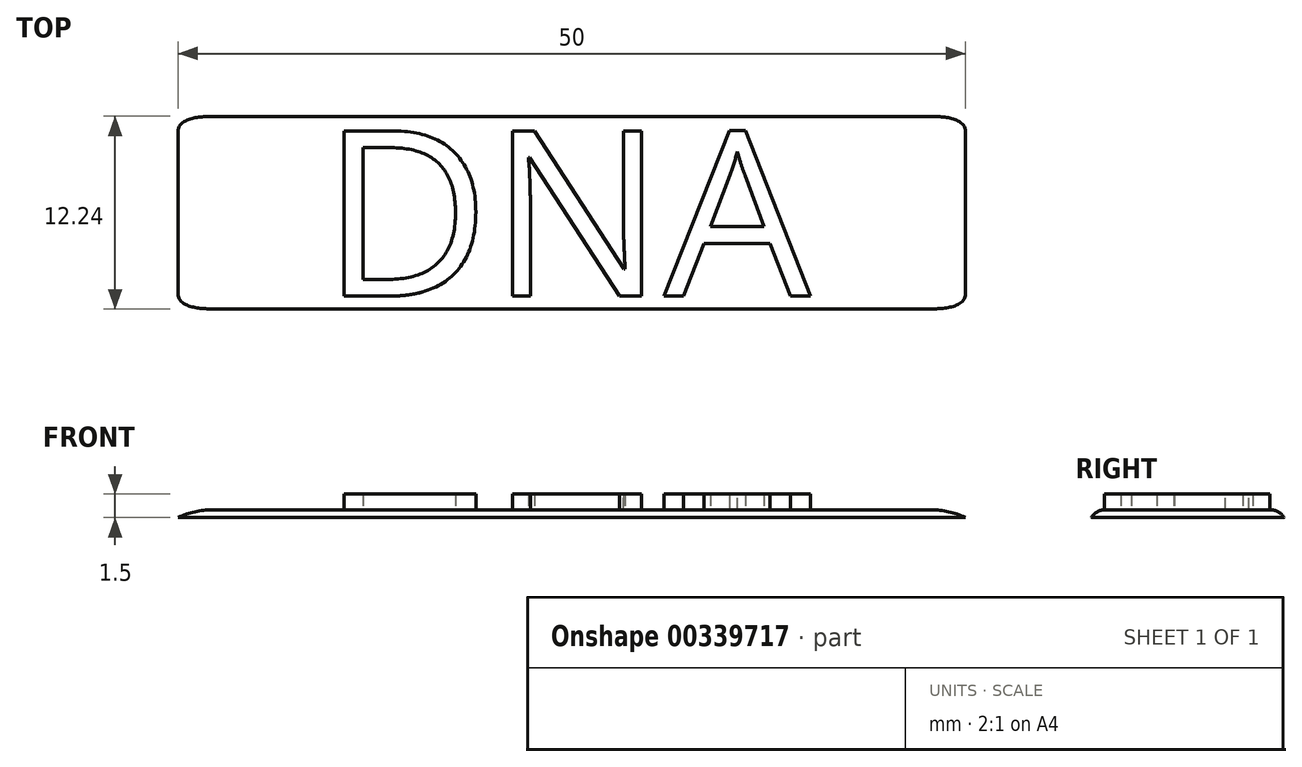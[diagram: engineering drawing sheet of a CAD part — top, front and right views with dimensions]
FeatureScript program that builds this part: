
annotation { "Feature Type Name" : "Feature", "Feature Type Description" : "" }
export const myFeature = defineFeature(function(context is Context, id is Id, definition is map)
    precondition{}
    {
        {
            var Q0;
            Q0=qCreatedBy(makeId("Top.planeOp"),FACE);
            var sketch = newSketch(context, id + "F0", { "sketchPlane" : qUnion([Q0])});
            skLineSegment(sketch, "E0.bottom", {"start": v(25, 6.25) * mm, "end": v(-25, 6.25) * mm});
            skLineSegment(sketch, "E0.top", {"start": v(25, -6.25) * mm, "end": v(-25, -6.25) * mm});
            skLineSegment(sketch, "E0.left", {"start": v(25, 6.25) * mm, "end": v(25, -6.25) * mm});
            skLineSegment(sketch, "E0.right", {"start": v(-25, 6.25) * mm, "end": v(-25, -6.25) * mm});
            skPoint(sketch, "E0.middle", {"position": v(0, 0) * mm});
            skText(sketch, "E1", { "text": "DNA\n", "fontName": "OpenSans-Regular.ttf"});
            skLineSegment(sketch, "E2", {"start": v(-15.9, 5.26) * mm, "end": v(16.1, -5.3) * mm, "construction": true});
            skLineSegment(sketch, "E3", {"start": v(16.1, 5.26) * mm, "end": v(-15.9, -5.3) * mm, "construction": true});
            const initialGuessF0  = {"E1": [-0.0159, -0.0053, 1, 0, 0.01057]};
            skSetInitialGuess(sketch, initialGuessF0);
            skSolve(sketch);
        }
        {
            var Q0;
            Q0=makeQuery(id+"F0.imprint","IMPRINT",FACE,{"disambiguationData":[TD([[makeQuery(id+"F0.imprint","IMPRINT",EDGE,{"derivedFrom":sQuery(id+"F0.wireOp",EDGE,"E0.bottom")}),1.0]])]});
            var sketch = newSketch(context, id + "F1", { "sketchPlane" : qUnion([Q0])});
            skLineSegment(sketch, "E4.bottom", {"start": v(25, 6.25) * mm, "end": v(-25, 6.25) * mm});
            skLineSegment(sketch, "E4.top", {"start": v(25, -6.25) * mm, "end": v(-25, -6.25) * mm});
            skLineSegment(sketch, "E4.left", {"start": v(25, 6.25) * mm, "end": v(25, -6.25) * mm});
            skLineSegment(sketch, "E4.right", {"start": v(-25, 6.25) * mm, "end": v(-25, -6.25) * mm});
            skPoint(sketch, "E4.middle", {"position": v(0, 0) * mm});
            skSolve(sketch);
        }
        {
            var Q0;
            Q0 = qSketchRegion(id + "F1", true);
            extrude(context, id + "F2", {"entities" : qUnion([Q0]), "oppositeDirection" : true, "depth" : .5 * mm});
        }
        {
            var Q0;
            Q0=makeQuery(id+"F0.imprint","IMPRINT",FACE,{"disambiguationData":[TD([[makeQuery(id+"F0.imprint","IMPRINT",EDGE,{"derivedFrom":sQuery(id+"F0.wireOp",EDGE,"E1.sketch_text.stroke-0")}),-1.0]])]});
            var Q1;
            Q1=makeQuery(id+"F0.imprint","IMPRINT",FACE,{"disambiguationData":[TD([[makeQuery(id+"F0.imprint","IMPRINT",EDGE,{"derivedFrom":sQuery(id+"F0.wireOp",EDGE,"E1.sketch_text.stroke-14")}),-1.0]])]});
            var Q2;
            Q2=makeQuery(id+"F0.imprint","IMPRINT",FACE,{"disambiguationData":[TD([[makeQuery(id+"F0.imprint","IMPRINT",EDGE,{"derivedFrom":sQuery(id+"F0.wireOp",EDGE,"E1.sketch_text.stroke-29")}),-1.0]])]});
            extrude(context, id + "F3", {"entities" : qUnion([Q0, Q1, Q2]), "operationType" : NewBodyOperationType.ADD, "depth" : 1 * mm});
        }
        {
            var Q0;
            Q0=makeQuery(id+"F2.opExtrude","CAP_EDGE",EDGE,{"disambiguationData":[OSD([sQuery(id+"F1.wireOp",EDGE,"E4.right")])],"isStart":true});
            var Q1;
            Q1=makeQuery(id+"F2.opExtrude","CAP_EDGE",EDGE,{"disambiguationData":[OSD([sQuery(id+"F1.wireOp",EDGE,"E4.left")])],"isStart":true});
            fillet(context, id + "F4", {"entities" : qUnion([Q0, Q1]), "radius" : 5 * mm, "tangentPropagation" : true, "allowEdgeOverflow" : false});
        }
        {
            var Q0;
            Q0=makeQuery(id+"F2.opExtrude","CAP_EDGE",EDGE,{"disambiguationData":[OSD([sQuery(id+"F1.wireOp",EDGE,"E4.bottom")])],"isStart":true});
            var Q1;
            Q1=makeQuery(id+"F4.opFillet","BLEND_EDGE",EDGE,{"blendedFrom":[makeQuery(id+"F2.opExtrude","CAP_EDGE",EDGE,{"disambiguationData":[OSD([sQuery(id+"F1.wireOp",EDGE,"E4.right")])],"isStart":true}),makeQuery(id+"F2.opExtrude","SWEPT_FACE",FACE,{"disambiguationData":[OSD([sQuery(id+"F1.wireOp",EDGE,"E4.top")])]})],"blendedInto":[makeQuery(id+"F2.opExtrude","SWEPT_FACE",FACE,{"disambiguationData":[OSD([sQuery(id+"F1.wireOp",EDGE,"E4.top")])]})]});
            var Q2;
            Q2=makeQuery(id+"F2.opExtrude","CAP_EDGE",EDGE,{"disambiguationData":[OSD([sQuery(id+"F1.wireOp",EDGE,"E4.top")])],"isStart":true});
            var Q3;
            Q3=makeQuery(id+"F4.opFillet","BLEND_EDGE",EDGE,{"blendedFrom":[makeQuery(id+"F2.opExtrude","CAP_EDGE",EDGE,{"disambiguationData":[OSD([sQuery(id+"F1.wireOp",EDGE,"E4.left")])],"isStart":true}),makeQuery(id+"F2.opExtrude","SWEPT_FACE",FACE,{"disambiguationData":[OSD([sQuery(id+"F1.wireOp",EDGE,"E4.top")])]})],"blendedInto":[makeQuery(id+"F2.opExtrude","SWEPT_FACE",FACE,{"disambiguationData":[OSD([sQuery(id+"F1.wireOp",EDGE,"E4.top")])]})]});
            var Q4;
            Q4=makeQuery(id+"F4.opFillet","BLEND_EDGE",EDGE,{"blendedFrom":[makeQuery(id+"F2.opExtrude","CAP_EDGE",EDGE,{"disambiguationData":[OSD([sQuery(id+"F1.wireOp",EDGE,"E4.left")])],"isStart":true}),makeQuery(id+"F2.opExtrude","SWEPT_FACE",FACE,{"disambiguationData":[OSD([sQuery(id+"F1.wireOp",EDGE,"E4.bottom")])]})],"blendedInto":[makeQuery(id+"F2.opExtrude","SWEPT_FACE",FACE,{"disambiguationData":[OSD([sQuery(id+"F1.wireOp",EDGE,"E4.bottom")])]})]});
            var Q5;
            Q5=makeQuery(id+"F4.opFillet","BLEND_EDGE",EDGE,{"blendedFrom":[makeQuery(id+"F2.opExtrude","CAP_EDGE",EDGE,{"disambiguationData":[OSD([sQuery(id+"F1.wireOp",EDGE,"E4.right")])],"isStart":true}),makeQuery(id+"F2.opExtrude","SWEPT_FACE",FACE,{"disambiguationData":[OSD([sQuery(id+"F1.wireOp",EDGE,"E4.bottom")])]})],"blendedInto":[makeQuery(id+"F2.opExtrude","SWEPT_FACE",FACE,{"disambiguationData":[OSD([sQuery(id+"F1.wireOp",EDGE,"E4.bottom")])]})]});
            fillet(context, id + "F5", {"entities" : qUnion([Q0, Q1, Q2, Q3, Q4, Q5]), "radius" : 1 * mm, "tangentPropagation" : true, "allowEdgeOverflow" : false});
        }
    });
